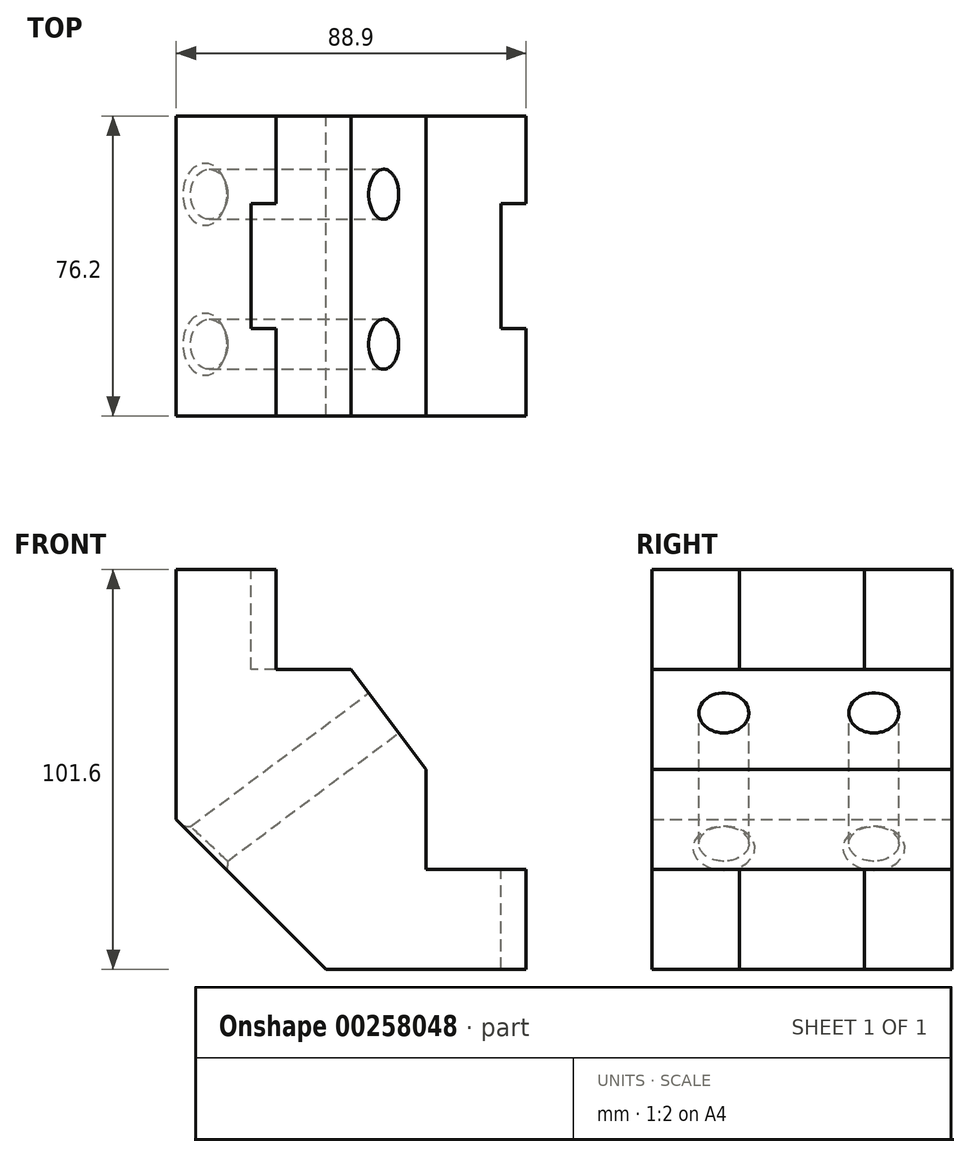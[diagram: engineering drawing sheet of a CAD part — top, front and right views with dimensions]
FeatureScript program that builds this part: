
annotation { "Feature Type Name" : "Feature", "Feature Type Description" : "" }
export const myFeature = defineFeature(function(context is Context, id is Id, definition is map)
    precondition{}
    {
        {
            var Q0;
            Q0=qCreatedBy(makeId("Front.planeOp"),FACE);
            var sketch = newSketch(context, id + "F0", { "sketchPlane" : qUnion([Q0])});
            skLineSegment(sketch, "E0", {"start": v(0, 25.4) * mm, "end": v(19.05, 0) * mm});
            skLineSegment(sketch, "E1", {"start": v(-44.45, 50.8) * mm, "end": v(-19.05, 50.8) * mm});
            skLineSegment(sketch, "E2", {"start": v(44.45, -50.8) * mm, "end": v(44.45, -25.4) * mm});
            skLineSegment(sketch, "E3", {"start": v(-19.05, 50.8) * mm, "end": v(-19.05, 25.4) * mm});
            skLineSegment(sketch, "E4", {"start": v(-19.05, 25.4) * mm, "end": v(0, 25.4) * mm});
            skLineSegment(sketch, "E5", {"start": v(19.05, 0) * mm, "end": v(19.05, -25.4) * mm});
            skLineSegment(sketch, "E6", {"start": v(44.45, -25.4) * mm, "end": v(19.05, -25.4) * mm});
            skLineSegment(sketch, "E7", {"start": v(44.45, -50.8) * mm, "end": v(-6.35, -50.8) * mm});
            skLineSegment(sketch, "E8", {"start": v(-6.35, -50.8) * mm, "end": v(-44.45, -12.7) * mm});
            skLineSegment(sketch, "E9", {"start": v(-44.45, 50.8) * mm, "end": v(-44.45, -12.7) * mm});
            skSolve(sketch);
        }
        {
            var Q0;
            Q0 = qSketchRegion(id + "F0", true);
            extrude(context, id + "F1", {"entities" : qUnion([Q0]), "endBound" : BoundingType.SYMMETRIC, "depth" : 76.2 * mm});
        }
        {
            var Q0;
            Q0=makeQuery(id+"F1.opExtrude","SWEPT_FACE",FACE,{"disambiguationData":[OSD([sQuery(id+"F0.wireOp",EDGE,"E0")])]});
            var sketch = newSketch(context, id + "F2", { "sketchPlane" : qUnion([Q0])});
            skCircle(sketch, "E10", {"center": v(-19.86, 6.53) * mm, "radius": 6.35 * mm});
            skCircle(sketch, "E11", {"center": v(18.24, 6.53) * mm, "radius": 6.35 * mm});
            skSolve(sketch);
        }
        {
            var Q0;
            Q0 = qSketchRegion(id + "F2", true);
            extrude(context, id + "F3", {"entities" : qUnion([Q0]), "operationType" : NewBodyOperationType.REMOVE, "endBound" : BoundingType.THROUGH_ALL, "oppositeDirection" : true, "depth" : 25.4 * mm});
        }
        {
            var Q0;
            Q0=makeQuery(id+"F1.opExtrude","SWEPT_FACE",FACE,{"disambiguationData":[OSD([sQuery(id+"F0.wireOp",EDGE,"E1")])]});
            var sketch = newSketch(context, id + "F4", { "sketchPlane" : qUnion([Q0])});
            skLineSegment(sketch, "E12", {"start": v(-19.05, -15.88) * mm, "end": v(-25.4, -15.88) * mm});
            skLineSegment(sketch, "E13", {"start": v(-25.4, -15.88) * mm, "end": v(-25.4, 15.88) * mm});
            skLineSegment(sketch, "E14", {"start": v(-25.4, 15.88) * mm, "end": v(-19.05, 15.88) * mm});
            skLineSegment(sketch, "E15", {"start": v(-19.05, 15.88) * mm, "end": v(-19.05, -15.88) * mm});
            skSolve(sketch);
        }
        {
            var Q0;
            Q0 = qSketchRegion(id + "F4", true);
            var Q1;
            Q1=makeQuery(id+"F1.opExtrude","SWEPT_FACE",FACE,{"disambiguationData":[OSD([sQuery(id+"F0.wireOp",EDGE,"E4")])]});
            extrude(context, id + "F5", {"entities" : qUnion([Q0]), "operationType" : NewBodyOperationType.REMOVE, "endBound" : BoundingType.UP_TO_SURFACE, "oppositeDirection" : true, "endBoundEntityFace" : qUnion([Q1]), "depth" : 25.4 * mm});
        }
        {
            var Q0;
            Q0=makeQuery(id+"F1.opExtrude","SWEPT_FACE",FACE,{"disambiguationData":[OSD([sQuery(id+"F0.wireOp",EDGE,"E6")])]});
            var sketch = newSketch(context, id + "F6", { "sketchPlane" : qUnion([Q0])});
            skLineSegment(sketch, "E16", {"start": v(44.45, -15.88) * mm, "end": v(38.1, -15.88) * mm});
            skLineSegment(sketch, "E17", {"start": v(38.1, -15.88) * mm, "end": v(38.1, 15.88) * mm});
            skLineSegment(sketch, "E18", {"start": v(38.1, 15.88) * mm, "end": v(44.45, 15.88) * mm});
            skLineSegment(sketch, "E19", {"start": v(44.45, 15.88) * mm, "end": v(44.45, -15.88) * mm});
            skSolve(sketch);
        }
        {
            var Q0;
            Q0=makeQuery(id+"F6.imprint","IMPRINT",FACE,{"disambiguationData":[TD([[makeQuery(id+"F6.imprint","IMPRINT",EDGE,{"derivedFrom":sQuery(id+"F6.wireOp",EDGE,"E16")}),-1.0]])]});
            extrude(context, id + "F7", {"entities" : qUnion([Q0]), "operationType" : NewBodyOperationType.REMOVE, "endBound" : BoundingType.THROUGH_ALL, "oppositeDirection" : true, "depth" : 25.4 * mm});
        }
        {
            var Q0;
            Q0=makeQuery(id+"F3.boolean.opBoolean","COPY",EDGE,{"derivedFrom":makeQuery(id+"F3.opExtrude","CAP_EDGE",EDGE,{"disambiguationData":[OSD([sQuery(id+"F2.wireOp",EDGE,"E10")])],"isStart":true})});
            var Q1;
            Q1=makeQuery(id+"F3.boolean.opBoolean","COPY",EDGE,{"derivedFrom":makeQuery(id+"F3.opExtrude","CAP_EDGE",EDGE,{"disambiguationData":[OSD([sQuery(id+"F2.wireOp",EDGE,"E11")])],"isStart":true})});
            var Q2;
            Q2=makeQuery(id+"F3.boolean.opBoolean","INTERSECT",EDGE,{"derivedFrom":[makeQuery(id+"F1.opExtrude","SWEPT_FACE",FACE,{"disambiguationData":[OSD([sQuery(id+"F0.wireOp",EDGE,"E8")])]}),makeQuery(id+"F3.opExtrude","SWEPT_FACE",FACE,{"disambiguationData":[OSD([sQuery(id+"F2.wireOp",EDGE,"E10")])]})]});
            var Q3;
            Q3=makeQuery(id+"F3.boolean.opBoolean","INTERSECT",EDGE,{"derivedFrom":[makeQuery(id+"F1.opExtrude","SWEPT_FACE",FACE,{"disambiguationData":[OSD([sQuery(id+"F0.wireOp",EDGE,"E8")])]}),makeQuery(id+"F3.opExtrude","SWEPT_FACE",FACE,{"disambiguationData":[OSD([sQuery(id+"F2.wireOp",EDGE,"E11")])]})]});
            chamfer(context, id + "F8", {"entities" : qUnion([Q0, Q1, Q2, Q3]), "width" : 1.52 * mm, "tangentPropagation" : true});
        }
    });
